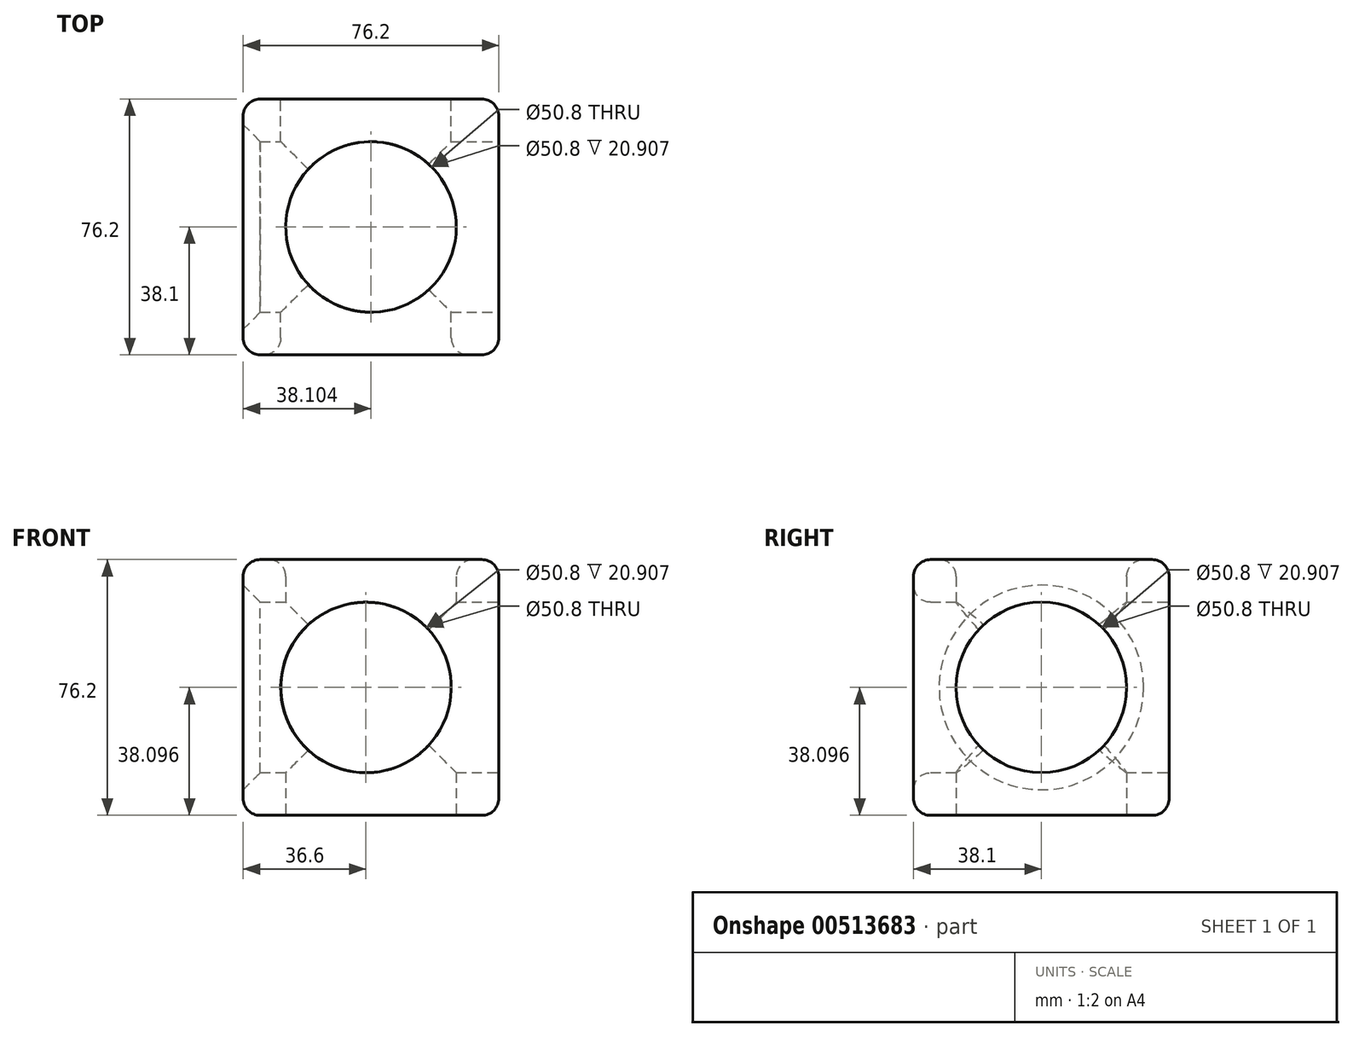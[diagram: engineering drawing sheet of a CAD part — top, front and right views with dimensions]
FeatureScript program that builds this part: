
annotation { "Feature Type Name" : "Feature", "Feature Type Description" : "" }
export const myFeature = defineFeature(function(context is Context, id is Id, definition is map)
    precondition{}
    {
        {
            var Q0;
            Q0=qCreatedBy(makeId("Front.planeOp"),FACE);
            var sketch = newSketch(context, id + "F0", { "sketchPlane" : qUnion([Q0])});
            skLineSegment(sketch, "E0.bottom", {"start": v(-36.6, 50.82) * mm, "end": v(39.6, 50.82) * mm});
            skLineSegment(sketch, "E0.top", {"start": v(-36.6, -25.38) * mm, "end": v(39.6, -25.38) * mm});
            skLineSegment(sketch, "E0.left", {"start": v(-36.6, 50.82) * mm, "end": v(-36.6, -25.38) * mm});
            skLineSegment(sketch, "E0.right", {"start": v(39.6, 50.82) * mm, "end": v(39.6, -25.38) * mm});
            skSolve(sketch);
        }
        {
            var Q0;
            Q0 = qSketchRegion(id + "F0", true);
            extrude(context, id + "F1", {"entities" : qUnion([Q0]), "depth" : 76.2 * mm});
        }
        {
            var Q0;
            Q0=makeQuery(id+"F1.opExtrude","SWEPT_FACE",FACE,{"disambiguationData":[OSD([sQuery(id+"F0.wireOp",EDGE,"E0.top")])]});
            var sketch = newSketch(context, id + "F2", { "sketchPlane" : qUnion([Q0])});
            skLineSegment(sketch, "E1", {"start": v(-36.6, 76.2) * mm, "end": v(39.6, 0) * mm, "construction": true});
            skCircle(sketch, "E2", {"center": v(1.5, 38.1) * mm, "radius": 25.4 * mm});
            skSolve(sketch);
        }
        {
            var Q0;
            Q0 = qSketchRegion(id + "F2", true);
            extrude(context, id + "F3", {"entities" : qUnion([Q0]), "operationType" : NewBodyOperationType.REMOVE, "endBound" : BoundingType.THROUGH_ALL, "oppositeDirection" : true, "depth" : 25.4 * mm});
        }
        {
            var Q0;
            Q0=makeQuery(id+"F1.opExtrude","CAP_FACE",FACE,{"disambiguationData":[OSD([sQuery(id+"F0.wireOp",EDGE,"E0.bottom"),sQuery(id+"F0.wireOp",EDGE,"E0.top"),sQuery(id+"F0.wireOp",EDGE,"E0.left"),sQuery(id+"F0.wireOp",EDGE,"E0.right")])],"isStart":true});
            var sketch = newSketch(context, id + "F4", { "sketchPlane" : qUnion([Q0])});
            skLineSegment(sketch, "E3", {"start": v(-39.6, 50.82) * mm, "end": v(36.6, -25.38) * mm});
            skCircle(sketch, "E4", {"center": v(0, 12.72) * mm, "radius": 25.4 * mm});
            skPoint(sketch, "E4.centerSnap0", {"position": v(-1.5, 12.72) * mm});
            skSolve(sketch);
        }
        {
            var Q0;
            Q0 = qSketchRegion(id + "F4", true);
            extrude(context, id + "F5", {"entities" : qUnion([Q0]), "operationType" : NewBodyOperationType.REMOVE, "endBound" : BoundingType.THROUGH_ALL, "oppositeDirection" : true, "depth" : 25.4 * mm});
        }
        {
            var Q0;
            Q0=makeQuery(id+"F1.opExtrude","SWEPT_FACE",FACE,{"disambiguationData":[OSD([sQuery(id+"F0.wireOp",EDGE,"E0.right")])]});
            var sketch = newSketch(context, id + "F6", { "sketchPlane" : qUnion([Q0])});
            skLineSegment(sketch, "E5", {"start": v(-76.2, 50.82) * mm, "end": v(0, -25.38) * mm, "construction": true});
            skCircle(sketch, "E6", {"center": v(-38.1, 12.72) * mm, "radius": 25.4 * mm});
            skSolve(sketch);
        }
        {
            var Q0;
            Q0 = qSketchRegion(id + "F6", true);
            extrude(context, id + "F7", {"entities" : qUnion([Q0]), "operationType" : NewBodyOperationType.REMOVE, "endBound" : BoundingType.THROUGH_ALL, "oppositeDirection" : true, "depth" : 25.4 * mm});
        }
        {
            var Q0;
            Q0=makeQuery(id+"F1.opExtrude","SWEPT_EDGE",EDGE,{"disambiguationData":[OSD([sQuery(id+"F0.wireOp",EDGE,"E0.bottom"),sQuery(id+"F0.wireOp",EDGE,"E0.right")])]});
            var Q1;
            Q1=makeQuery(id+"F1.opExtrude","CAP_EDGE",EDGE,{"disambiguationData":[OSD([sQuery(id+"F0.wireOp",EDGE,"E0.right")])],"isStart":false});
            var Q2;
            Q2=makeQuery(id+"F1.opExtrude","SWEPT_EDGE",EDGE,{"disambiguationData":[OSD([sQuery(id+"F0.wireOp",EDGE,"E0.top"),sQuery(id+"F0.wireOp",EDGE,"E0.right")])]});
            var Q3;
            Q3=makeQuery(id+"F1.opExtrude","CAP_EDGE",EDGE,{"disambiguationData":[OSD([sQuery(id+"F0.wireOp",EDGE,"E0.right")])],"isStart":true});
            var Q4;
            Q4=makeQuery(id+"F7.boolean.opBoolean","COPY",EDGE,{"derivedFrom":makeQuery(id+"F7.opExtrude","CAP_EDGE",EDGE,{"disambiguationData":[OSD([sQuery(id+"F6.wireOp",EDGE,"E6")])],"isStart":true})});
            var Q5;
            Q5=makeQuery(id+"F5.boolean.opBoolean","COPY",EDGE,{"derivedFrom":makeQuery(id+"F5.opExtrude","CAP_EDGE",EDGE,{"disambiguationData":[OSD([sQuery(id+"F4.wireOp",EDGE,"E4")])],"isStart":true})});
            var Q6;
            Q6=makeQuery(id+"F1.opExtrude","CAP_EDGE",EDGE,{"disambiguationData":[OSD([sQuery(id+"F0.wireOp",EDGE,"E0.left")])],"isStart":true});
            var Q7;
            Q7=makeQuery(id+"F1.opExtrude","CAP_EDGE",EDGE,{"disambiguationData":[OSD([sQuery(id+"F0.wireOp",EDGE,"E0.bottom")])],"isStart":true});
            var Q8;
            Q8=makeQuery(id+"F1.opExtrude","CAP_EDGE",EDGE,{"disambiguationData":[OSD([sQuery(id+"F0.wireOp",EDGE,"E0.top")])],"isStart":true});
            var Q9;
            Q9=makeQuery(id+"F3.boolean.opBoolean","COPY",EDGE,{"derivedFrom":makeQuery(id+"F3.opExtrude","CAP_EDGE",EDGE,{"disambiguationData":[OSD([sQuery(id+"F2.wireOp",EDGE,"E2")])],"isStart":true})});
            var Q10;
            Q10=makeQuery(id+"F1.opExtrude","CAP_EDGE",EDGE,{"disambiguationData":[OSD([sQuery(id+"F0.wireOp",EDGE,"E0.top")])],"isStart":false});
            var Q11;
            Q11=makeQuery(id+"F1.opExtrude","SWEPT_EDGE",EDGE,{"disambiguationData":[OSD([sQuery(id+"F0.wireOp",EDGE,"E0.top"),sQuery(id+"F0.wireOp",EDGE,"E0.left")])]});
            var Q12;
            Q12=makeQuery(id+"F1.opExtrude","SWEPT_EDGE",EDGE,{"disambiguationData":[OSD([sQuery(id+"F0.wireOp",EDGE,"E0.bottom"),sQuery(id+"F0.wireOp",EDGE,"E0.left")])]});
            var Q13;
            Q13=makeQuery(id+"F1.opExtrude","CAP_EDGE",EDGE,{"disambiguationData":[OSD([sQuery(id+"F0.wireOp",EDGE,"E0.bottom")])],"isStart":false});
            var Q14;
            Q14=makeQuery(id+"F3.boolean.opBoolean","INTERSECT",EDGE,{"derivedFrom":[makeQuery(id+"F1.opExtrude","SWEPT_FACE",FACE,{"disambiguationData":[OSD([sQuery(id+"F0.wireOp",EDGE,"E0.bottom")])]}),makeQuery(id+"F3.opExtrude","SWEPT_FACE",FACE,{"disambiguationData":[OSD([sQuery(id+"F2.wireOp",EDGE,"E2")])]})]});
            var Q15;
            Q15=makeQuery(id+"F5.boolean.opBoolean","INTERSECT",EDGE,{"derivedFrom":[makeQuery(id+"F1.opExtrude","CAP_FACE",FACE,{"disambiguationData":[OSD([sQuery(id+"F0.wireOp",EDGE,"E0.bottom"),sQuery(id+"F0.wireOp",EDGE,"E0.top"),sQuery(id+"F0.wireOp",EDGE,"E0.left"),sQuery(id+"F0.wireOp",EDGE,"E0.right")])],"isStart":false}),makeQuery(id+"F5.opExtrude","SWEPT_FACE",FACE,{"disambiguationData":[OSD([sQuery(id+"F4.wireOp",EDGE,"E4")])]})]});
            var Q16;
            Q16=makeQuery(id+"F1.opExtrude","CAP_EDGE",EDGE,{"disambiguationData":[OSD([sQuery(id+"F0.wireOp",EDGE,"E0.left")])],"isStart":false});
            fillet(context, id + "F8", {"entities" : qUnion([Q0, Q1, Q2, Q3, Q4, Q5, Q6, Q7, Q8, Q9, Q10, Q11, Q12, Q13, Q14, Q15, Q16]), "radius" : 5.08 * mm, "tangentPropagation" : true, "allowEdgeOverflow" : false});
        }
        {
            var Q0;
            Q0=makeQuery(id+"F7.boolean.opBoolean","INTERSECT",EDGE,{"derivedFrom":[makeQuery(id+"F1.opExtrude","SWEPT_FACE",FACE,{"disambiguationData":[OSD([sQuery(id+"F0.wireOp",EDGE,"E0.left")])]}),makeQuery(id+"F7.opExtrude","SWEPT_FACE",FACE,{"disambiguationData":[OSD([sQuery(id+"F6.wireOp",EDGE,"E6")])]})]});
            chamfer(context, id + "F9", {"entities" : qUnion([Q0]), "width" : 5.08 * mm, "tangentPropagation" : true});
        }
    });
